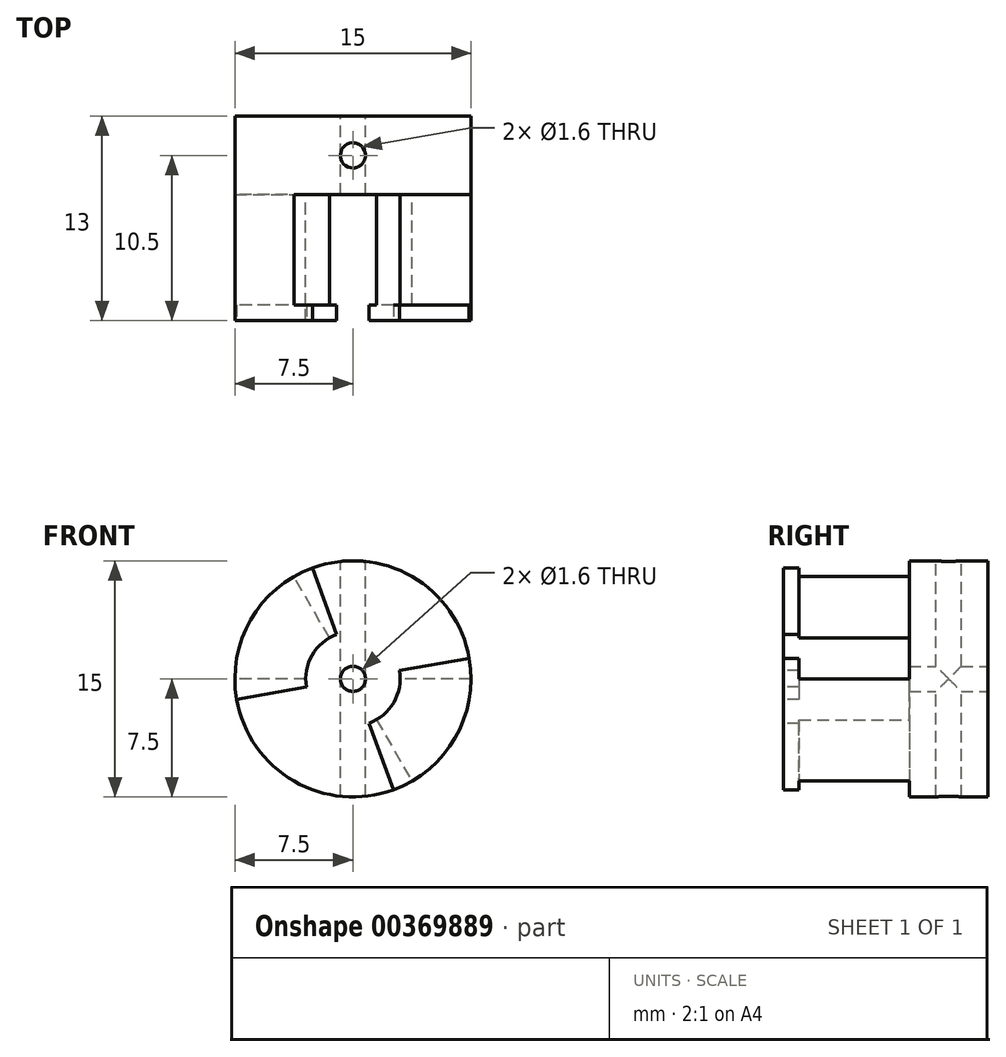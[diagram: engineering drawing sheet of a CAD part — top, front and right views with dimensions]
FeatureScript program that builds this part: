
annotation { "Feature Type Name" : "Feature", "Feature Type Description" : "" }
export const myFeature = defineFeature(function(context is Context, id is Id, definition is map)
    precondition{}
    {
        {
            var Q0;
            Q0=qCreatedBy(makeId("Front.planeOp"),FACE);
            var sketch = newSketch(context, id + "F0", { "sketchPlane" : qUnion([Q0])});
            skCircle(sketch, "E0", {"center": v(0, 0) * mm, "radius": 7.5 * mm});
            skSolve(sketch);
        }
        {
            var Q0;
            Q0=makeQuery(id+"F0.imprint","IMPRINT",FACE,{"disambiguationData":[TD([[makeQuery(id+"F0.imprint","IMPRINT",EDGE,{"derivedFrom":sQuery(id+"F0.wireOp",EDGE,"E0")}),1.0]])]});
            extrude(context, id + "F1", {"entities" : qUnion([Q0]), "offsetDistance" : 25 * mm, "depth" : 5 * mm});
        }
        {
            var Q0;
            Q0=makeQuery(id+"F1.opExtrude","CAP_FACE",FACE,{"disambiguationData":[OSD([sQuery(id+"F0.wireOp",EDGE,"E0")])],"isStart":false});
            var sketch = newSketch(context, id + "F2", { "sketchPlane" : qUnion([Q0])});
            skLineSegment(sketch, "E1", {"start": v(0, 7.5) * mm, "end": v(0, -7.5) * mm, "construction": true});
            skLineSegment(sketch, "E2", {"start": v(-7.5, 0) * mm, "end": v(7.5, 0) * mm, "construction": true});
            skLineSegment(sketch, "E3", {"start": v(-3.75, 6.5) * mm, "end": v(3.75, -6.5) * mm, "construction": true});
            skLineSegment(sketch, "E4", {"start": v(6.5, 3.75) * mm, "end": v(-6.5, -3.75) * mm, "construction": true});
            skPoint(sketch, "E5", {"position": v(0, 0) * mm});
            skArc(sketch, "E6", {"start": v(-1.5, 2.6) * mm, "mid": v(-2.6, 1.5) * mm, "end": v(-3, 0) * mm});
            skArc(sketch, "E7.0", {"start": v(-3.75, 6.5) * mm, "mid": v(-6.5, 3.75) * mm, "end": v(-7.5, 0) * mm});
            skLineSegment(sketch, "E8", {"start": v(-1.5, 2.6) * mm, "end": v(-3.75, 6.5) * mm});
            skLineSegment(sketch, "E9", {"start": v(-3, 0) * mm, "end": v(-7.5, 0) * mm});
            skLineSegment(sketch, "E10", {"start": v(1.5, -2.6) * mm, "end": v(3.75, -6.5) * mm});
            skLineSegment(sketch, "E11", {"start": v(7.5, 0) * mm, "end": v(3, 0) * mm});
            skArc(sketch, "E12.trimOffspring", {"start": v(3.75, -6.5) * mm, "mid": v(6.5, -3.75) * mm, "end": v(7.5, 0) * mm});
            skArc(sketch, "E13.trimOffspring", {"start": v(1.5, -2.6) * mm, "mid": v(2.6, -1.5) * mm, "end": v(3, 0) * mm});
            skSolve(sketch);
        }
        {
            var Q0;
            Q0 = qSketchRegion(id + "F2", true);
            extrude(context, id + "F3", {"entities" : qUnion([Q0]), "operationType" : NewBodyOperationType.ADD, "depth" : 8 * mm});
        }
        {
            var Q0;
            Q0=makeQuery(id+"F1.opExtrude","CAP_FACE",FACE,{"disambiguationData":[OSD([sQuery(id+"F0.wireOp",EDGE,"E0")])],"isStart":true});
            var sketch = newSketch(context, id + "F4", { "sketchPlane" : qUnion([Q0])});
            skCircle(sketch, "E14", {"center": v(0, 0) * mm, "radius": 0.8 * mm});
            skSolve(sketch);
        }
        {
            var Q0;
            Q0 = qSketchRegion(id + "F4", true);
            extrude(context, id + "F5", {"entities" : qUnion([Q0]), "operationType" : NewBodyOperationType.REMOVE, "endBound" : BoundingType.THROUGH_ALL, "oppositeDirection" : true, "depth" : 40.3 * mm});
        }
        {
            var Q0;
            Q0=qCreatedBy(makeId("Top.planeOp"),FACE);
            var sketch = newSketch(context, id + "F6", { "sketchPlane" : qUnion([Q0])});
            skCircle(sketch, "E15", {"center": v(0, -2.5) * mm, "radius": 0.8 * mm});
            skSolve(sketch);
        }
        {
            var Q0;
            Q0 = qSketchRegion(id + "F6", true);
            extrude(context, id + "F7", {"entities" : qUnion([Q0]), "operationType" : NewBodyOperationType.REMOVE, "endBound" : BoundingType.SYMMETRIC, "oppositeDirection" : true, "depth" : 25 * mm});
        }
        {
            var Q0;
            Q0=makeQuery(id+"F3.opExtrude","CAP_FACE",FACE,{"disambiguationData":[OSD([sQuery(id+"F2.wireOp",EDGE,"E6"),sQuery(id+"F2.wireOp",EDGE,"E7.0"),sQuery(id+"F2.wireOp",EDGE,"E8"),sQuery(id+"F2.wireOp",EDGE,"E9")])],"isStart":false});
            var sketch = newSketch(context, id + "F8", { "sketchPlane" : qUnion([Q0])});
            skArc(sketch, "E16", {"start": v(1.03, -2.82) * mm, "mid": v(2.6, -1.5) * mm, "end": v(2.96, 0.52) * mm});
            skLineSegment(sketch, "E17", {"start": v(7.39, 1.3) * mm, "end": v(2.96, 0.52) * mm});
            skLineSegment(sketch, "E18", {"start": v(2.57, -7.05) * mm, "end": v(1.03, -2.82) * mm});
            skLineSegment(sketch, "E19.trimOffspring", {"start": v(-2.95, -0.52) * mm, "end": v(-7.39, -1.3) * mm});
            skLineSegment(sketch, "E20.trimOffspring", {"start": v(-1.03, 2.82) * mm, "end": v(-2.56, 7.05) * mm});
            skArc(sketch, "E21.trimOffspring", {"start": v(-1.03, 2.82) * mm, "mid": v(-2.6, 1.5) * mm, "end": v(-2.95, -0.52) * mm});
            skArc(sketch, "E22", {"start": v(-2.56, 7.05) * mm, "mid": v(-6.5, 3.75) * mm, "end": v(-7.39, -1.3) * mm});
            skArc(sketch, "E23.trimOffspring", {"start": v(2.57, -7.05) * mm, "mid": v(6.5, -3.75) * mm, "end": v(7.39, 1.3) * mm});
            skSolve(sketch);
        }
        {
            var Q0;
            Q0 = qSketchRegion(id + "F8", true);
            extrude(context, id + "F9", {"entities" : qUnion([Q0]), "operationType" : NewBodyOperationType.ADD, "oppositeDirection" : true, "depth" : 1 * mm});
        }
    });
